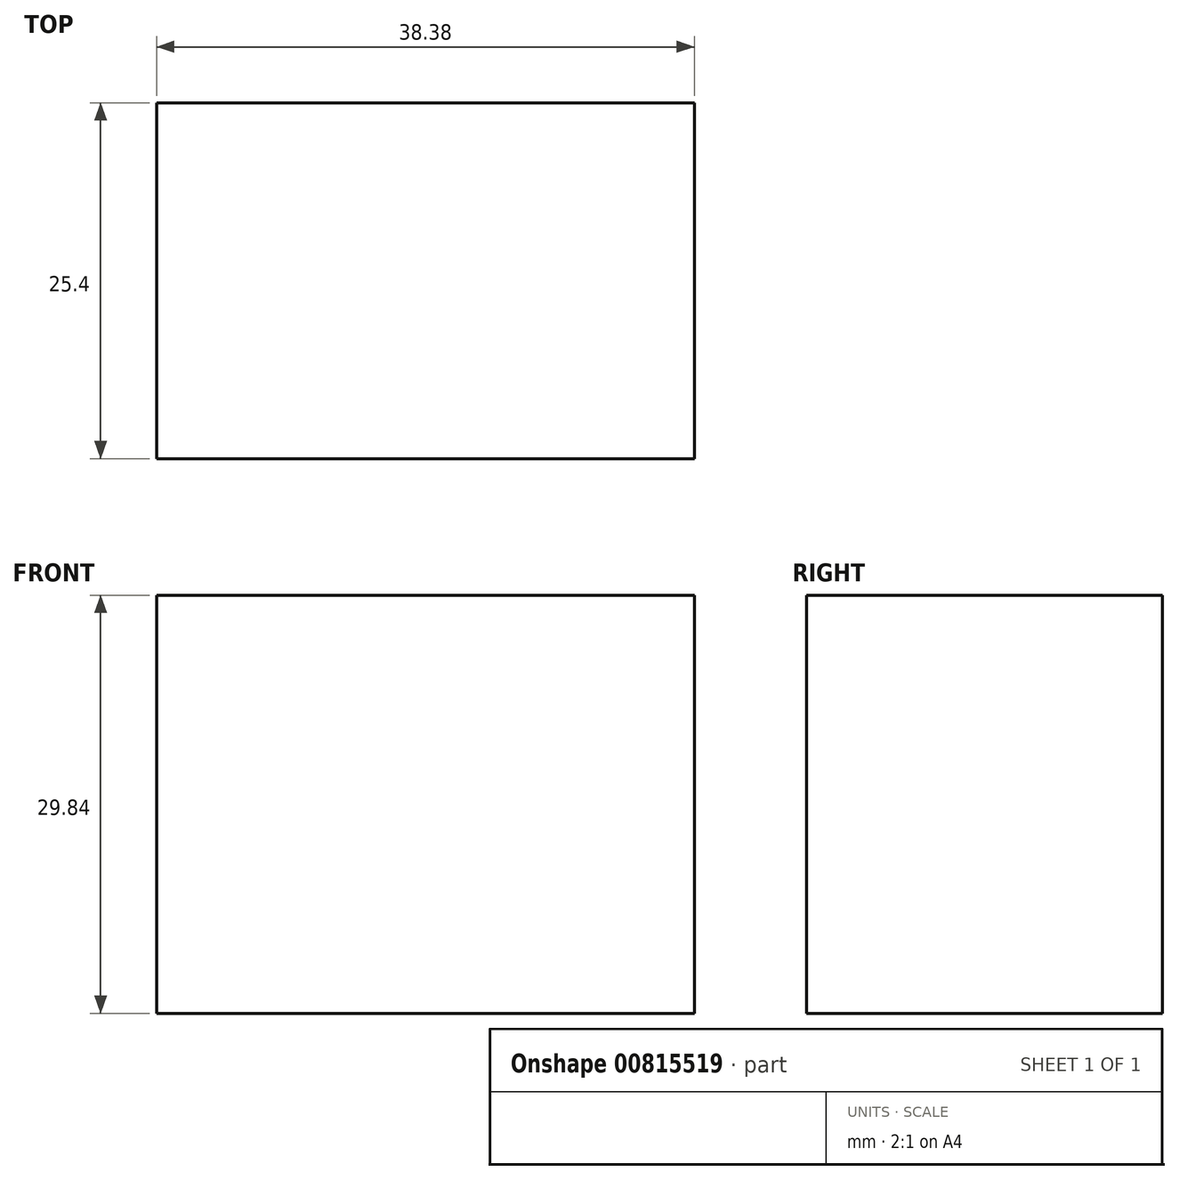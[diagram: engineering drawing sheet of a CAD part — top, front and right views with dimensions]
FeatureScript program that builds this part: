
annotation { "Feature Type Name" : "Feature", "Feature Type Description" : "" }
export const myFeature = defineFeature(function(context is Context, id is Id, definition is map)
    precondition{}
    {
        {
            var Q0;
            Q0=qCreatedBy(makeId("Front.planeOp"),FACE);
            var sketch = newSketch(context, id + "F0", { "sketchPlane" : qUnion([Q0])});
            skLineSegment(sketch, "E0.bottom", {"start": v(14.68, 0) * mm, "end": v(0, 0) * mm});
            skLineSegment(sketch, "E0.top", {"start": v(14.68, 0) * mm, "end": v(0, 0) * mm});
            skLineSegment(sketch, "E0.left", {"start": v(14.68, 0) * mm, "end": v(14.68, 0) * mm});
            skLineSegment(sketch, "E0.right", {"start": v(0, 0) * mm, "end": v(0, 0) * mm});
            skLineSegment(sketch, "E1.bottom", {"start": v(-17.97, 42.5) * mm, "end": v(-14.11, 42.5) * mm});
            skLineSegment(sketch, "E1.top", {"start": v(-17.97, 34.6) * mm, "end": v(-14.11, 34.6) * mm});
            skLineSegment(sketch, "E1.left", {"start": v(-17.97, 42.5) * mm, "end": v(-17.97, 34.6) * mm});
            skLineSegment(sketch, "E1.right", {"start": v(-14.11, 42.5) * mm, "end": v(-14.11, 34.6) * mm});
            skLineSegment(sketch, "E2.bottom", {"start": v(24.27, 4.75) * mm, "end": v(-14.11, 4.75) * mm});
            skLineSegment(sketch, "E2.top", {"start": v(24.27, 34.6) * mm, "end": v(-14.11, 34.6) * mm});
            skLineSegment(sketch, "E2.left", {"start": v(24.27, 4.75) * mm, "end": v(24.27, 34.6) * mm});
            skLineSegment(sketch, "E2.right", {"start": v(-14.11, 4.75) * mm, "end": v(-14.11, 34.6) * mm});
            skSolve(sketch);
        }
        {
            var Q0;
            Q0=makeQuery(id+"F0.imprint","IMPRINT",FACE,{"disambiguationData":[TD([[makeQuery(id+"F0.imprint","IMPRINT",EDGE,{"derivedFrom":sQuery(id+"F0.wireOp",EDGE,"E2.bottom")}),-1.0]])]});
            extrude(context, id + "F1", {"entities" : qUnion([Q0]), "depth" : 25.4 * mm, "offsetDistance" : 25.4 * mm});
        }
    });
